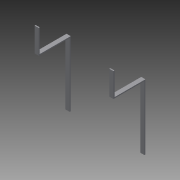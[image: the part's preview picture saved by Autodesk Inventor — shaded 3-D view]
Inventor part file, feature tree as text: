
AUTODESK INVENTOR PART (.ipt)
format: ipt  version: 2013 (Build 170138000, 138)  size: 148,992 bytes
history: native  units: in
note: dims shown in document units (in); Inventor stores cm internally (conversion verified against a paired STEP export)
features: extrude x8, sketch x8
ambient origin geometry x8: Origin, YZ Plane, XZ Plane, XY Plane, X Axis, Y Axis, Z Axis, Center Point
bodies: Solid1 (feature_tree)
feature tree (16):
  extrude  "Extrusion1"  Depth=3.0in
  extrude  "Extrusion2"  Depth=16.8in
  extrude  "Extrusion3"  Depth=16.8in
  extrude  "Extrusion4"  Depth=1.0in
  extrude  "Extrusion5"  Depth=1.0in
  extrude  "Extrusion6"  Depth=0.75in TaperAngle=0.0deg
  extrude  "Extrusion7"  Depth=19.0in
  extrude  "Extrusion8"  Depth=0.5in
  sketch  "Sketch1"  dims[d0=3.0in d1=3.0in]
  sketch  "Sketch2"  dims[d2=3.6in d3=16.8in]
  sketch  "Sketch3"  dims[d4=3.6in d5=16.8in]
  sketch  "Sketch4"  dims[d6=19.0in d7=1.0in]
  sketch  "Sketch5"  dims[d8=19.0in d9=1.0in]
  sketch  "Sketch6"  dims[d10=19.0in d11=0.75in d12=0.0in]
  sketch  "Sketch7"  dims[d13=0.5in d14=19.0in]
  sketch  "Sketch8"  dims[d15=82.3125in d16=0.0in d17=0.5in d18=0.5in d19=7.375in d20=0.25in d21=0.25in d22=15.25in d23=18.8in d24=0.0in d25=26.95in d26=0.0in d27=39.675in d28=0.0in d29=7.3875in d30=0.0in d31=2.0in d32=0.0in d33=2.0in d34=0.0in]
